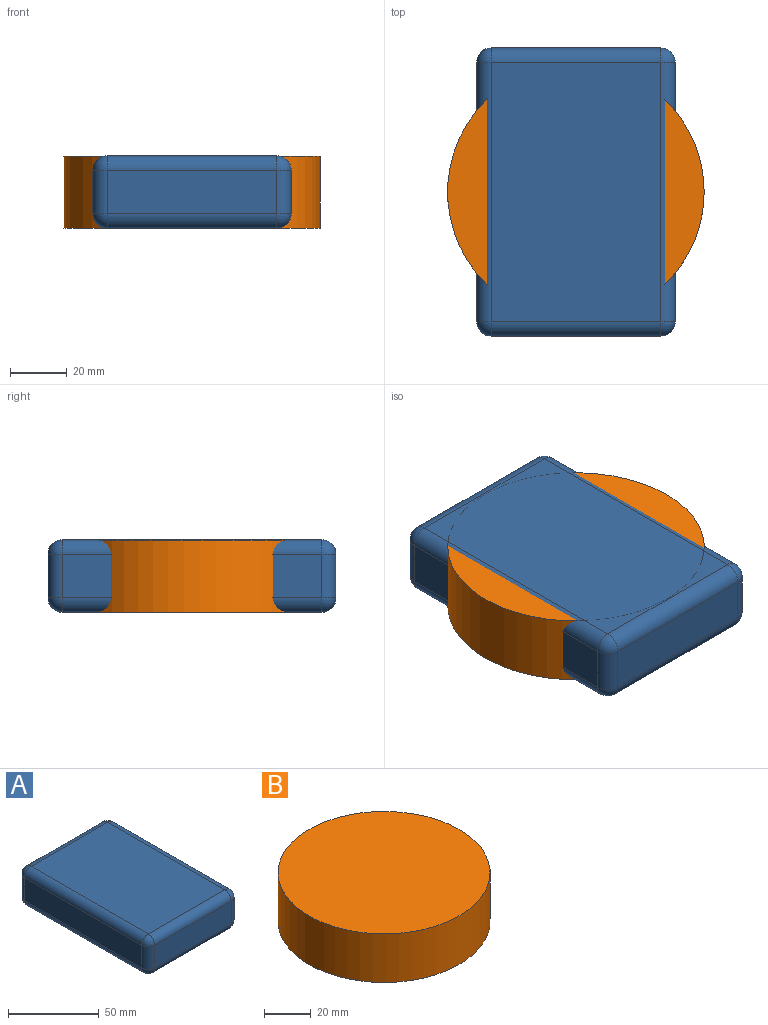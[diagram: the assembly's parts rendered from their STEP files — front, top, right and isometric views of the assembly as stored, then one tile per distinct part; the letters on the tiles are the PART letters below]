
ASSEMBLY  parts=2 mates=1
PART A: 26 faces, bbox 70x101.6x25.7 mm
  f0: plane 59.85x15.49mm, normal (0,-1,0), area 927.4mm2, adj f8,f9,f11,f12
  f1: plane 91.44x15.49mm, normal (1,0,0), area 1416.8mm2, adj f6,f11,f18,f20
  f2: plane 59.85x15.49mm, normal (0,1,0), area 927.4mm2, adj f14,f16,f18,f22
  f3: plane 91.44x15.49mm, normal (-1,0,0), area 1416.8mm2, adj f7,f8,f14,f24
  f4: plane 91.44x59.85mm, normal (0,0,1), area 5473.1mm2, adj f6,f7,f12,f16
  f5: plane 91.44x59.85mm, normal (0,0,-1), area 5473.1mm2, adj f9,f20,f22,f24
  f6: cylinder r=5.08mm len=91.44mm, axis (0,-1,0), area 729.7mm2, adj f1,f4,f13,f17
  f7: cylinder r=5.08mm len=91.44mm, axis (0,1,0), area 729.7mm2, adj f3,f4,f10,f15
  f8: cylinder r=5.08mm len=15.49mm, axis (0,0,1), area 123.6mm2, adj f0,f3,f10,f25
  f9: cylinder r=5.08mm len=59.85mm, axis (1,0,0), area 477.6mm2, adj f0,f5,f19,f25
  f10: sphere r=5.08mm, area 40.5mm2, adj f7,f8,f12
  f11: cylinder r=5.08mm len=15.49mm, axis (0,0,-1), area 123.6mm2, adj f0,f1,f13,f19
  f12: cylinder r=5.08mm len=59.85mm, axis (-1,0,0), area 477.6mm2, adj f0,f4,f10,f13
  f13: sphere r=5.08mm, area 40.5mm2, adj f6,f11,f12
  f14: cylinder r=5.08mm len=15.49mm, axis (0,0,-1), area 123.6mm2, adj f2,f3,f15,f23
  f15: sphere r=5.08mm, area 40.5mm2, adj f7,f14,f16
  f16: cylinder r=5.08mm len=59.85mm, axis (1,0,0), area 477.6mm2, adj f2,f4,f15,f17
  f17: sphere r=5.08mm, area 40.5mm2, adj f6,f16,f18
  f18: cylinder r=5.08mm len=15.49mm, axis (0,0,1), area 123.6mm2, adj f1,f2,f17,f21
  f19: sphere r=5.08mm, area 40.5mm2, adj f9,f11,f20
  f20: cylinder r=5.08mm len=91.44mm, axis (0,1,0), area 729.7mm2, adj f1,f5,f19,f21
  f21: sphere r=5.08mm, area 40.5mm2, adj f18,f20,f22
  f22: cylinder r=5.08mm len=59.85mm, axis (-1,0,0), area 477.6mm2, adj f2,f5,f21,f23
  f23: sphere r=5.08mm, area 40.5mm2, adj f14,f22,f24
  f24: cylinder r=5.08mm len=91.44mm, axis (0,-1,0), area 729.7mm2, adj f3,f5,f23,f25
  f25: sphere r=5.08mm, area 40.5mm2, adj f8,f9,f24
PART B: 3 faces, bbox 90.5x90.5x25.4 mm
  f0: cylinder r=45.26mm len=90.51mm, axis (0,0,-1), area 7222.6mm2, adj f1,f2
  f1: plane 90.51x90.51mm, normal (0,0,1), area 6434.5mm2, adj f0
  f2: plane 90.51x90.51mm, normal (0,0,-1), area 6434.5mm2, adj f0
PLACE A t=(-109.39,-67.9,-7.11)mm
PLACE B t=(-144.4,-118.7,-7.11)mm
MATE fastened B.f0 <-> A.f5  axis (0,0,-1) through (-144.4,-118.7,-7.11)mm
